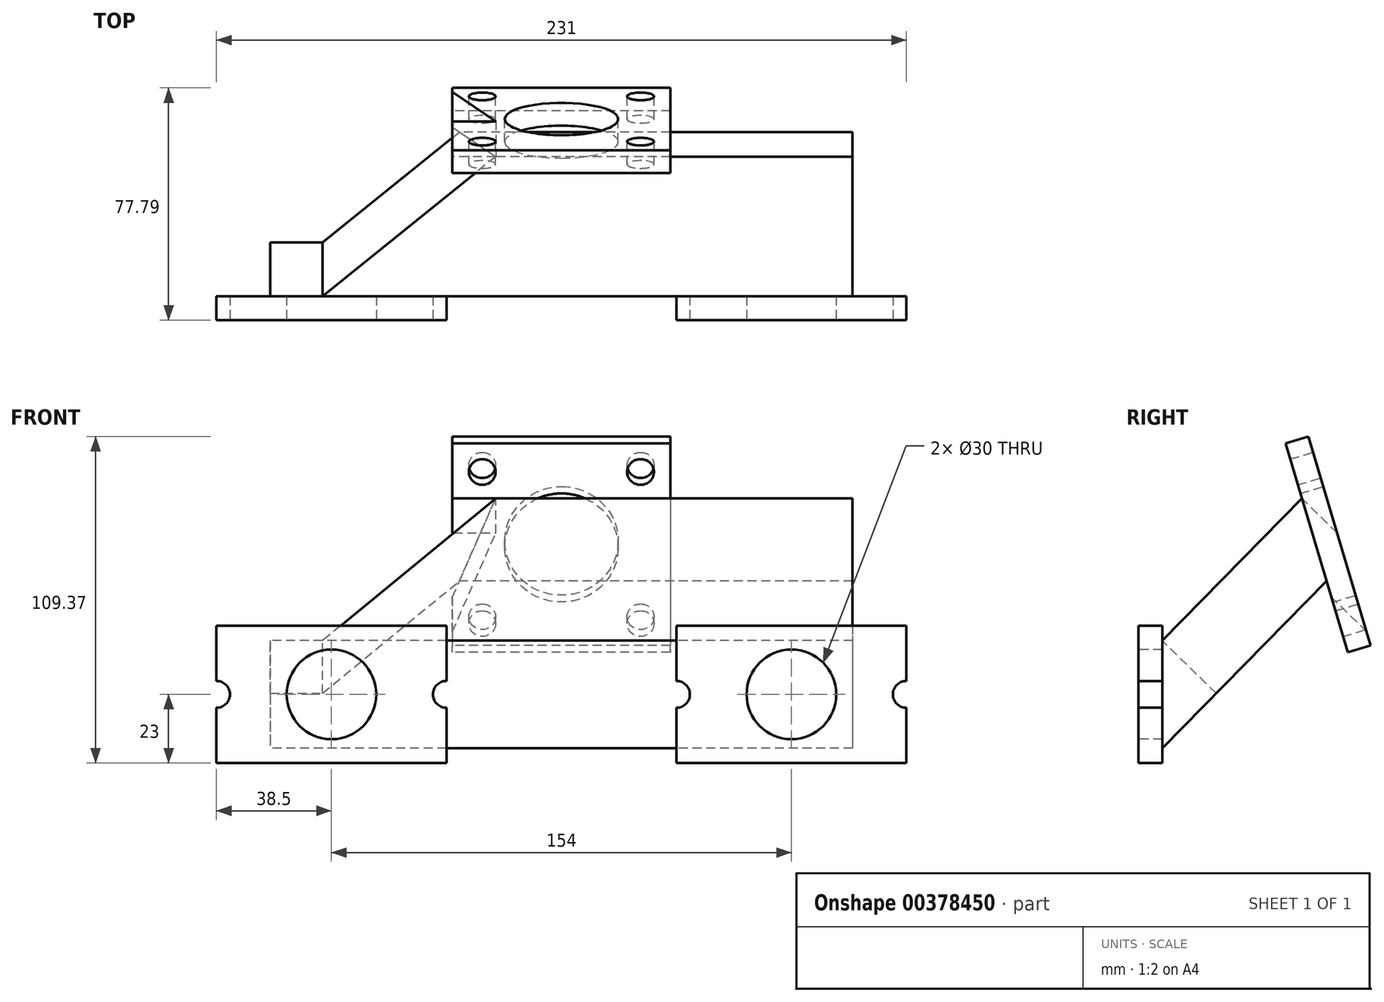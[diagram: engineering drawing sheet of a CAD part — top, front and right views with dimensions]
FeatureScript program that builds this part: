
annotation { "Feature Type Name" : "Feature", "Feature Type Description" : "" }
export const myFeature = defineFeature(function(context is Context, id is Id, definition is map)
    precondition{}
    {
        {
            var Q0;
            Q0=qCreatedBy(makeId("Front.planeOp"),FACE);
            var sketch = newSketch(context, id + "F0", { "sketchPlane" : qUnion([Q0])});
            skCircle(sketch, "E0", {"center": v(-77, 0) * mm, "radius": 15 * mm});
            skCircle(sketch, "E1", {"center": v(77, 0) * mm, "radius": 15 * mm});
            skLineSegment(sketch, "E2.bottom", {"start": v(-115.5, 23) * mm, "end": v(-38.5, 23) * mm});
            skLineSegment(sketch, "E2.top", {"start": v(-115.5, -23) * mm, "end": v(-38.5, -23) * mm});
            skLineSegment(sketch, "E2.left", {"start": v(-115.5, 23) * mm, "end": v(-115.5, 4.5) * mm});
            skLineSegment(sketch, "E2.right", {"start": v(-38.5, 23) * mm, "end": v(-38.5, 4.5) * mm});
            skLineSegment(sketch, "E3.bottom", {"start": v(38.5, 23) * mm, "end": v(115.5, 23) * mm});
            skLineSegment(sketch, "E3.top", {"start": v(38.5, -23) * mm, "end": v(115.5, -23) * mm});
            skLineSegment(sketch, "E3.left", {"start": v(38.5, 23) * mm, "end": v(38.5, 4.5) * mm});
            skLineSegment(sketch, "E3.right", {"start": v(115.5, 23) * mm, "end": v(115.5, 4.5) * mm});
            skArc(sketch, "E4", {"start": v(-38.5, 4.5) * mm, "mid": v(-43, 0) * mm, "end": v(-38.5, -4.5) * mm});
            skArc(sketch, "E5", {"start": v(-115.5, -4.5) * mm, "mid": v(-111, 0) * mm, "end": v(-115.5, 4.5) * mm});
            skArc(sketch, "E6", {"start": v(38.5, -4.5) * mm, "mid": v(43, 0) * mm, "end": v(38.5, 4.5) * mm});
            skArc(sketch, "E7", {"start": v(115.5, 4.5) * mm, "mid": v(111, 0) * mm, "end": v(115.5, -4.5) * mm});
            skLineSegment(sketch, "E8.trimOffspring", {"start": v(-38.5, -4.5) * mm, "end": v(-38.5, -23) * mm});
            skLineSegment(sketch, "E9.trimOffspring", {"start": v(-115.5, -4.5) * mm, "end": v(-115.5, -23) * mm});
            skLineSegment(sketch, "E10.trimOffspring", {"start": v(38.5, -4.5) * mm, "end": v(38.5, -23) * mm});
            skLineSegment(sketch, "E11.trimOffspring", {"start": v(115.5, -4.5) * mm, "end": v(115.5, -23) * mm});
            skSolve(sketch);
        }
        {
            var Q0;
            Q0=makeQuery(id+"F0.imprint","IMPRINT",FACE,{"disambiguationData":[TD([[makeQuery(id+"F0.imprint","IMPRINT",EDGE,{"derivedFrom":sQuery(id+"F0.wireOp",EDGE,"E0")}),-1.0]])]});
            var Q1;
            Q1=makeQuery(id+"F0.imprint","IMPRINT",FACE,{"disambiguationData":[TD([[makeQuery(id+"F0.imprint","IMPRINT",EDGE,{"derivedFrom":sQuery(id+"F0.wireOp",EDGE,"E1")}),-1.0]])]});
            extrude(context, id + "F1", {"entities" : qUnion([Q0, Q1]), "oppositeDirection" : true, "depth" : 8 * mm});
        }
        {
            var Q0;
            Q0=makeQuery(id+"F1.opExtrude","CAP_EDGE",EDGE,{"disambiguationData":[OSD([sQuery(id+"F0.wireOp",EDGE,"E3.bottom")])],"isStart":false});
            cPlane(context, id + "F2", {"entities" : qUnion([Q0]), "cplaneType" : CPlaneType.LINE_ANGLE, "offset" : 25 * mm, "angle" : 16.6 * degree, "width" : 150 * mm, "height" : 150 * mm});
        }
        {
            var Q0;
            Q0=qCreatedBy(id+"F2.planeOp",FACE);
            cPlane(context, id + "F3", {"entities" : qUnion([Q0]), "cplaneType" : CPlaneType.OFFSET, "offset" : 65 * mm, "width" : 150 * mm, "height" : 150 * mm});
        }
        {
            var Q0;
            Q0=qCreatedBy(id+"F3.planeOp",FACE);
            var sketch = newSketch(context, id + "F4", { "sketchPlane" : qUnion([Q0])});
            skCircle(sketch, "E12", {"center": v(0, 30) * mm, "radius": 19 * mm});
            skLineSegment(sketch, "E13.bottom", {"start": v(-36.5, 66.5) * mm, "end": v(36.5, 66.5) * mm});
            skLineSegment(sketch, "E13.top", {"start": v(-36.5, -6.5) * mm, "end": v(36.5, -6.5) * mm});
            skLineSegment(sketch, "E13.left", {"start": v(-36.5, 66.5) * mm, "end": v(-36.5, -6.5) * mm});
            skLineSegment(sketch, "E13.right", {"start": v(36.5, 66.5) * mm, "end": v(36.5, -6.5) * mm});
            skCircle(sketch, "E14", {"center": v(-26.5, 56.5) * mm, "radius": 4.5 * mm});
            skCircle(sketch, "E15", {"center": v(26.5, 56.5) * mm, "radius": 4.5 * mm});
            skCircle(sketch, "E16", {"center": v(26.5, 3.5) * mm, "radius": 4.5 * mm});
            skCircle(sketch, "E17", {"center": v(-26.5, 3.5) * mm, "radius": 4.5 * mm});
            skSolve(sketch);
        }
        {
            var Q0;
            Q0=makeQuery(id+"F4.imprint","IMPRINT",FACE,{"disambiguationData":[TD([[makeQuery(id+"F4.imprint","IMPRINT",EDGE,{"derivedFrom":sQuery(id+"F4.wireOp",EDGE,"E12")}),-1.0]])]});
            extrude(context, id + "F5", {"entities" : qUnion([Q0]), "oppositeDirection" : true, "depth" : 8 * mm});
        }
        {
            var Q0;
            Q0=qCreatedBy(makeId("Right.planeOp"),FACE);
            var sketch = newSketch(context, id + "F6", { "sketchPlane" : qUnion([Q0])});
            skLineSegment(sketch, "E18", {"start": v(54.77, 65.64) * mm, "end": v(8, 18) * mm});
            skLineSegment(sketch, "E19", {"start": v(63, 38.03) * mm, "end": v(8, -18) * mm});
            skLineSegment(sketch, "E20", {"start": v(8, 18) * mm, "end": v(8, -18) * mm});
            skLineSegment(sketch, "E21", {"start": v(54.77, 65.64) * mm, "end": v(63, 38.03) * mm});
            skSolve(sketch);
        }
        {
            var Q0;
            Q0 = qSketchRegion(id + "F6", true);
            extrude(context, id + "F7", {"entities" : qUnion([Q0]), "endBound" : BoundingType.SYMMETRIC, "depth" : 195 * mm});
        }
        {
            var Q0;
            Q0=makeQuery(id+"F7.opExtrude","SWEPT_FACE",FACE,{"disambiguationData":[OSD([sQuery(id+"F6.wireOp",EDGE,"E18")])]});
            var sketch = newSketch(context, id + "F8", { "sketchPlane" : qUnion([Q0])});
            skLineSegment(sketch, "E22", {"start": v(-22, 85.2) * mm, "end": v(-80, 18.45) * mm});
            skLineSegment(sketch, "E23", {"start": v(-80, 18.45) * mm, "end": v(-97.5, 18.45) * mm});
            skLineSegment(sketch, "E24", {"start": v(-97.5, 18.45) * mm, "end": v(-97.5, 85.2) * mm});
            skLineSegment(sketch, "E25", {"start": v(-97.5, 85.2) * mm, "end": v(-22, 85.2) * mm});
            skSolve(sketch);
        }
        {
            var Q0;
            Q0=makeQuery(id+"F8.imprint","IMPRINT",FACE,{"disambiguationData":[TD([[makeQuery(id+"F8.imprint","IMPRINT",EDGE,{"derivedFrom":sQuery(id+"F8.wireOp",EDGE,"E22")}),-1.0]])]});
            extrude(context, id + "F9", {"entities" : qUnion([Q0]), "operationType" : NewBodyOperationType.REMOVE, "endBound" : BoundingType.THROUGH_ALL, "oppositeDirection" : true, "depth" : 25 * mm});
        }
    });
